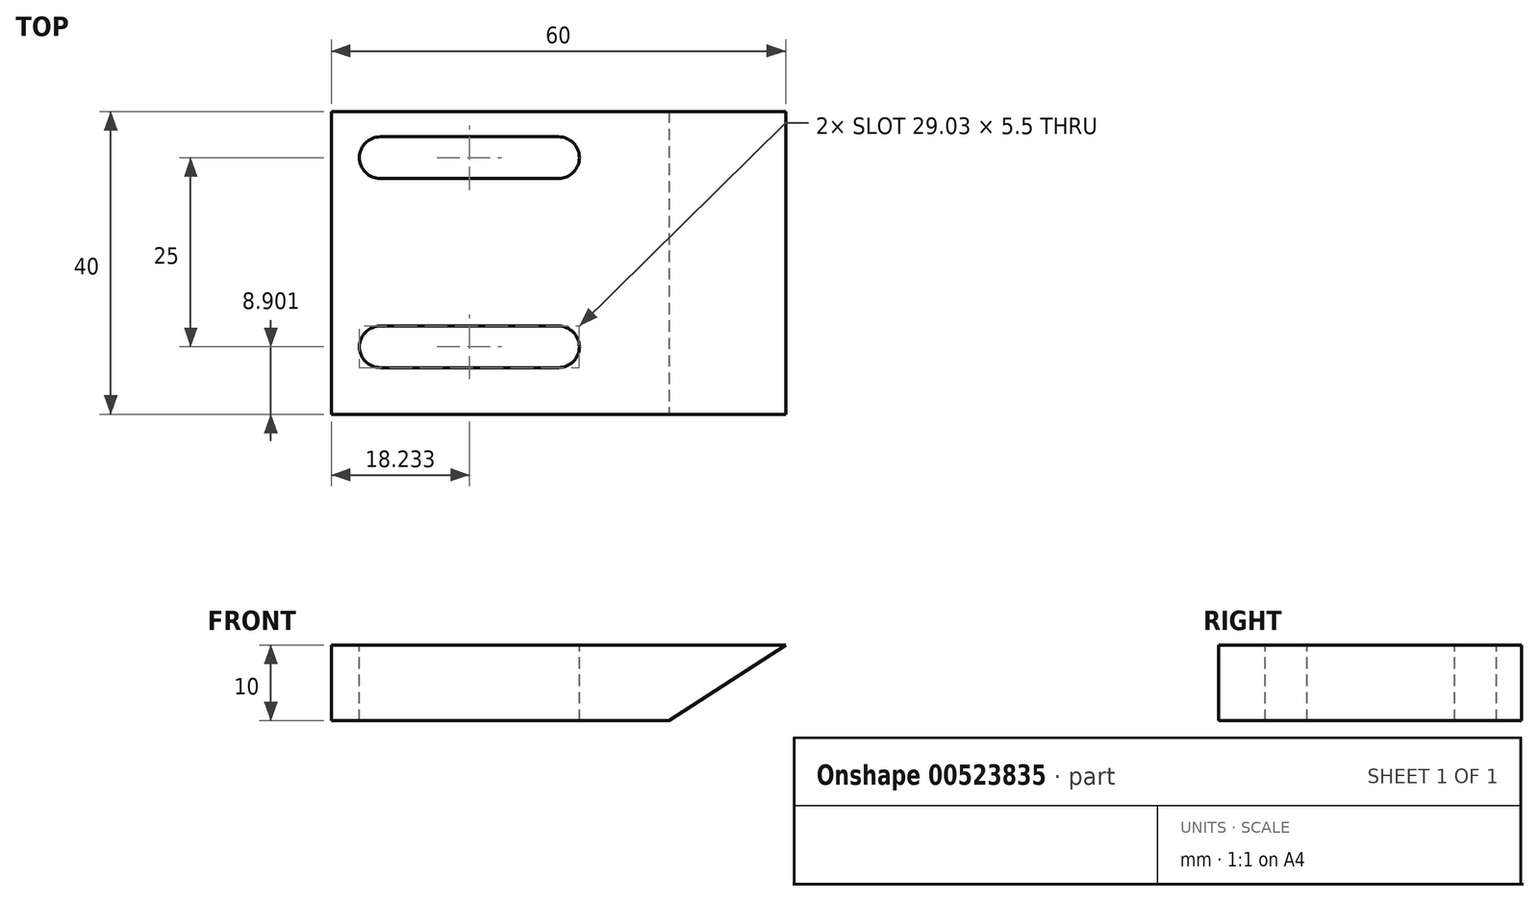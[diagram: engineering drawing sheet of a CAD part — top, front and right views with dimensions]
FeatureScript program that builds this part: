
annotation { "Feature Type Name" : "Feature", "Feature Type Description" : "" }
export const myFeature = defineFeature(function(context is Context, id is Id, definition is map)
    precondition{}
    {
        {
            var Q0;
            Q0=qCreatedBy(makeId("Top.planeOp"),FACE);
            var sketch = newSketch(context, id + "F0", { "sketchPlane" : qUnion([Q0])});
            skLineSegment(sketch, "E0.bottom", {"start": v(30, 20) * mm, "end": v(-30, 20) * mm});
            skLineSegment(sketch, "E0.top", {"start": v(30, -20) * mm, "end": v(-30, -20) * mm});
            skLineSegment(sketch, "E0.left", {"start": v(30, 20) * mm, "end": v(30, -20) * mm});
            skLineSegment(sketch, "E0.right", {"start": v(-30, 20) * mm, "end": v(-30, -20) * mm});
            skPoint(sketch, "E0.middle", {"position": v(0, 0) * mm});
            skSolve(sketch);
        }
        {
            var Q0;
            Q0=makeQuery(id+"F0.imprint","IMPRINT",FACE,{"disambiguationData":[TD([[makeQuery(id+"F0.imprint","IMPRINT",EDGE,{"derivedFrom":sQuery(id+"F0.wireOp",EDGE,"E0.bottom")}),1.0]])]});
            extrude(context, id + "F1", {"entities" : qUnion([Q0]), "depth" : 10 * mm, "offsetDistance" : 25 * mm});
        }
        {
            var Q0;
            Q0=makeQuery(id+"F1.opExtrude","CAP_FACE",FACE,{"disambiguationData":[OSD([sQuery(id+"F0.wireOp",EDGE,"E0.bottom"),sQuery(id+"F0.wireOp",EDGE,"E0.top"),sQuery(id+"F0.wireOp",EDGE,"E0.left"),sQuery(id+"F0.wireOp",EDGE,"E0.right")])],"isStart":false});
            var sketch = newSketch(context, id + "F2", { "sketchPlane" : qUnion([Q0])});
            skPoint(sketch, "E1", {"position": v(0, 13.9) * mm});
            skPoint(sketch, "E2", {"position": v(0, -11.1) * mm});
            skLineSegment(sketch, "E3", {"start": v(0, 13.9) * mm, "end": v(-23.53, 13.9) * mm});
            skLineSegment(sketch, "E4", {"start": v(0, -11.1) * mm, "end": v(-23.53, -11.1) * mm});
            skArc(sketch, "E5.0.startCap", {"start": v(0, 16.65) * mm, "mid": v(2.75, 13.9) * mm, "end": v(0, 11.15) * mm});
            skArc(sketch, "E5.0.endCap", {"start": v(-23.53, 11.15) * mm, "mid": v(-26.28, 13.9) * mm, "end": v(-23.53, 16.65) * mm});
            skLineSegment(sketch, "E5.0.left", {"start": v(0, 11.15) * mm, "end": v(-23.53, 11.15) * mm});
            skLineSegment(sketch, "E5.0.right", {"start": v(0, 16.65) * mm, "end": v(-23.53, 16.65) * mm});
            skArc(sketch, "E6.0.startCap", {"start": v(0, -8.35) * mm, "mid": v(2.75, -11.1) * mm, "end": v(0, -13.85) * mm});
            skArc(sketch, "E6.0.endCap", {"start": v(-23.53, -13.85) * mm, "mid": v(-26.28, -11.1) * mm, "end": v(-23.53, -8.35) * mm});
            skLineSegment(sketch, "E6.0.left", {"start": v(0, -13.85) * mm, "end": v(-23.53, -13.85) * mm});
            skLineSegment(sketch, "E6.0.right", {"start": v(0, -8.35) * mm, "end": v(-23.53, -8.35) * mm});
            skSolve(sketch);
        }
        {
            var Q0;
            Q0=makeQuery(id+"F1.opExtrude","SWEPT_FACE",FACE,{"disambiguationData":[OSD([sQuery(id+"F0.wireOp",EDGE,"E0.top")])]});
            var sketch = newSketch(context, id + "F3", { "sketchPlane" : qUnion([Q0])});
            skLineSegment(sketch, "E7", {"start": v(14.6, 10) * mm, "end": v(0, 0) * mm});
            skLineSegment(sketch, "E8", {"start": v(0, 0) * mm, "end": v(0, -12.97) * mm});
            skLineSegment(sketch, "E9", {"start": v(30, 10) * mm, "end": v(0, -12.97) * mm});
            skLineSegment(sketch, "E10", {"start": v(30, 10) * mm, "end": v(14.6, 10) * mm});
            skSolve(sketch);
        }
        {
            var Q0;
            Q0=makeQuery(id+"F3.imprint","IMPRINT",FACE,{"disambiguationData":[TD([[makeQuery(id+"F3.imprint","IMPRINT",EDGE,{"derivedFrom":sQuery(id+"F3.wireOp",EDGE,"E7")}),-1.0]])]});
            extrude(context, id + "F4", {"entities" : qUnion([Q0]), "operationType" : NewBodyOperationType.ADD, "oppositeDirection" : true, "depth" : 40 * mm, "offsetDistance" : 25 * mm});
        }
        {
            var Q0;
            Q0 = qSketchRegion(id + "F2", true);
            extrude(context, id + "F5", {"entities" : qUnion([Q0]), "operationType" : NewBodyOperationType.REMOVE, "oppositeDirection" : true, "depth" : 25 * mm, "offsetDistance" : 25 * mm});
        }
        {
            var Q0;
            Q0=makeQuery(id+"F4.boolean.opBoolean","MERGE",FACE,{"derivedFrom":[makeQuery(id+"F1.opExtrude","SWEPT_FACE",FACE,{"disambiguationData":[OSD([sQuery(id+"F0.wireOp",EDGE,"E0.top")])]}),makeQuery(id+"F4.opExtrude","CAP_FACE",FACE,{"disambiguationData":[OSD([sQuery(id+"F3.wireOp",EDGE,"E7"),sQuery(id+"F3.wireOp",EDGE,"E8"),sQuery(id+"F3.wireOp",EDGE,"E9"),sQuery(id+"F3.wireOp",EDGE,"E10")])],"isStart":true})]});
            var sketch = newSketch(context, id + "F6", { "sketchPlane" : qUnion([Q0])});
            skLineSegment(sketch, "E11", {"start": v(30, 10) * mm, "end": v(14.6, 0) * mm});
            skLineSegment(sketch, "E12", {"start": v(14.6, 0) * mm, "end": v(30, 0) * mm});
            skLineSegment(sketch, "E13", {"start": v(30, 0) * mm, "end": v(30, 10) * mm});
            skSolve(sketch);
        }
        {
            var Q0;
            Q0 = qSketchRegion(id + "F6", true);
            extrude(context, id + "F7", {"entities" : qUnion([Q0]), "operationType" : NewBodyOperationType.REMOVE, "oppositeDirection" : true, "depth" : 40 * mm, "offsetDistance" : 25 * mm});
        }
    });
